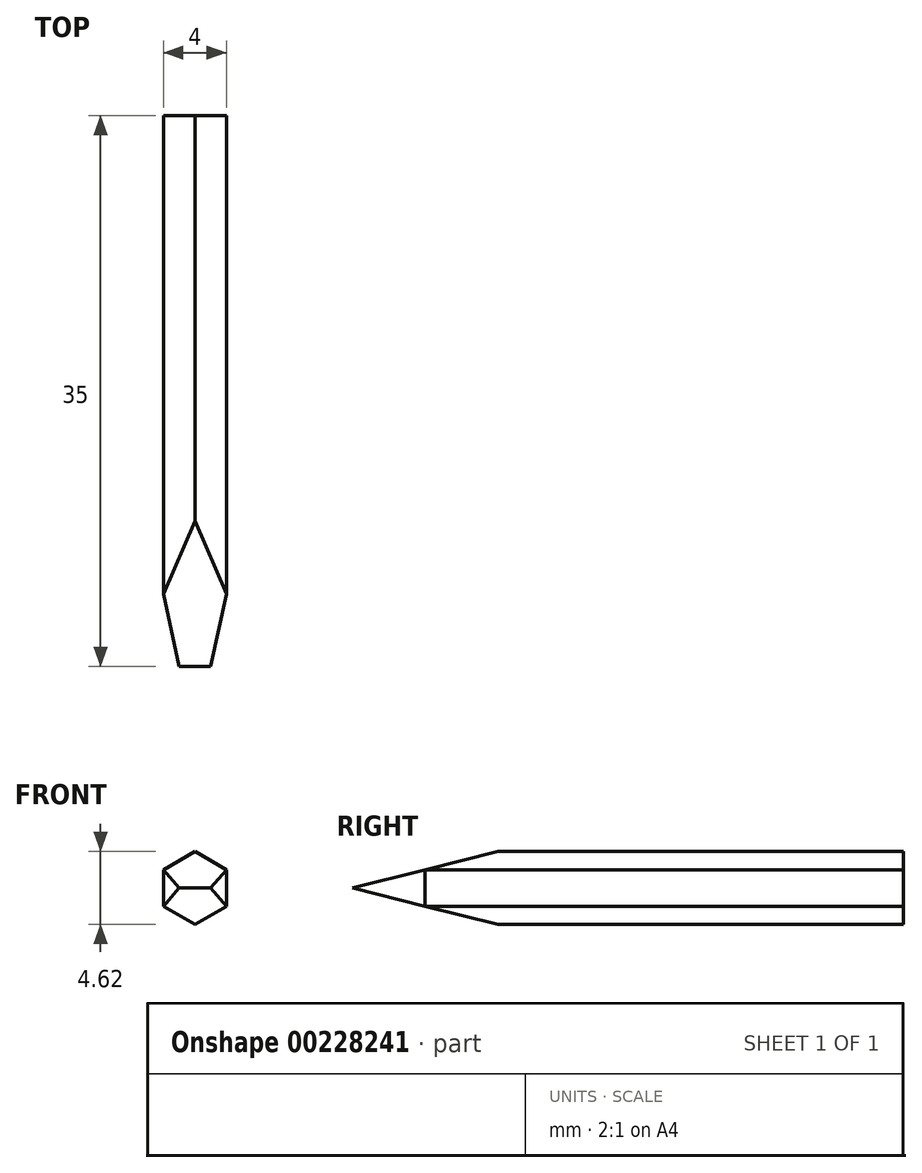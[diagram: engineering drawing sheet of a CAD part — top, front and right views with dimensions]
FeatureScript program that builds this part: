
annotation { "Feature Type Name" : "Feature", "Feature Type Description" : "" }
export const myFeature = defineFeature(function(context is Context, id is Id, definition is map)
    precondition{}
    {
        {
            var Q0;
            Q0=qCreatedBy(makeId("Front.planeOp"),FACE);
            var sketch = newSketch(context, id + "F0", { "sketchPlane" : qUnion([Q0])});
            skCircle(sketch, "E0.cCircle", {"center": v(-8.62, 0) * mm, "radius": 2 * mm, "construction": true});
            skLineSegment(sketch, "E0.0", {"start": v(-6.62, 1.15) * mm, "end": v(-6.62, -1.15) * mm});
            skLineSegment(sketch, "E0.1", {"start": v(-6.62, -1.15) * mm, "end": v(-8.62, -2.3) * mm});
            skLineSegment(sketch, "E0.2", {"start": v(-8.62, -2.3) * mm, "end": v(-10.62, -1.15) * mm});
            skLineSegment(sketch, "E0.3", {"start": v(-10.62, -1.15) * mm, "end": v(-10.62, 1.15) * mm});
            skLineSegment(sketch, "E0.4", {"start": v(-10.62, 1.15) * mm, "end": v(-8.62, 2.3) * mm});
            skLineSegment(sketch, "E0.5", {"start": v(-8.62, 2.3) * mm, "end": v(-6.62, 1.15) * mm});
            skPoint(sketch, "E0.0.midPoint", {"position": v(-6.62, 0) * mm});
            skSolve(sketch);
        }
        {
            var Q0;
            Q0 = qSketchRegion(id + "F0", true);
            extrude(context, id + "F1", {"entities" : qUnion([Q0]), "depth" : 35 * mm});
        }
        {
            var Q0;
            Q0=makeQuery(id+"F1.opExtrude","SWEPT_FACE",FACE,{"disambiguationData":[OSD([sQuery(id+"F0.wireOp",EDGE,"E0.0")])]});
            var sketch = newSketch(context, id + "F2", { "sketchPlane" : qUnion([Q0])});
            skLineSegment(sketch, "E1", {"start": v(-35, 0) * mm, "end": v(-35, 2.5) * mm});
            skLineSegment(sketch, "E2", {"start": v(-35, 2.5) * mm, "end": v(-25, 2.5) * mm});
            skLineSegment(sketch, "E3", {"start": v(-25, 2.5) * mm, "end": v(-35, 0) * mm});
            skLineSegment(sketch, "E4", {"start": v(-35, 0) * mm, "end": v(-35, -2.5) * mm});
            skLineSegment(sketch, "E5", {"start": v(-35, -2.5) * mm, "end": v(-25, -2.5) * mm});
            skLineSegment(sketch, "E6", {"start": v(-25, -2.5) * mm, "end": v(-35, 0) * mm});
            skSolve(sketch);
        }
        {
            var Q0;
            Q0 = qSketchRegion(id + "F2", true);
            extrude(context, id + "F3", {"entities" : qUnion([Q0]), "operationType" : NewBodyOperationType.REMOVE, "endBound" : BoundingType.THROUGH_ALL, "oppositeDirection" : true, "depth" : 25 * mm});
        }
        {
            var Q0;
            Q0=qCreatedBy(makeId("Top.planeOp"),FACE);
            var sketch = newSketch(context, id + "F4", { "sketchPlane" : qUnion([Q0])});
            skLineSegment(sketch, "E7", {"start": v(-6.62, -30.38) * mm, "end": v(-7.62, -35) * mm});
            skLineSegment(sketch, "E8", {"start": v(-7.62, -35) * mm, "end": v(-6.62, -35) * mm});
            skLineSegment(sketch, "E9", {"start": v(-6.62, -35) * mm, "end": v(-6.62, -30.38) * mm});
            skLineSegment(sketch, "E10", {"start": v(-9.62, -35) * mm, "end": v(-10.62, -35) * mm});
            skLineSegment(sketch, "E11", {"start": v(-10.62, -35) * mm, "end": v(-10.62, -30.38) * mm});
            skLineSegment(sketch, "E12", {"start": v(-10.62, -30.38) * mm, "end": v(-9.62, -35) * mm});
            skSolve(sketch);
        }
        {
            var Q0;
            Q0 = qSketchRegion(id + "F4", true);
            extrude(context, id + "F5", {"entities" : qUnion([Q0]), "operationType" : NewBodyOperationType.REMOVE, "endBound" : BoundingType.THROUGH_ALL, "oppositeDirection" : true, "depth" : 25 * mm, "hasSecondDirection" : true, "secondDirectionBound" : SecondDirectionBoundingType.THROUGH_ALL, "secondDirectionOppositeDirection" : false, "secondDirectionDepth" : 25 * mm});
        }
    });
